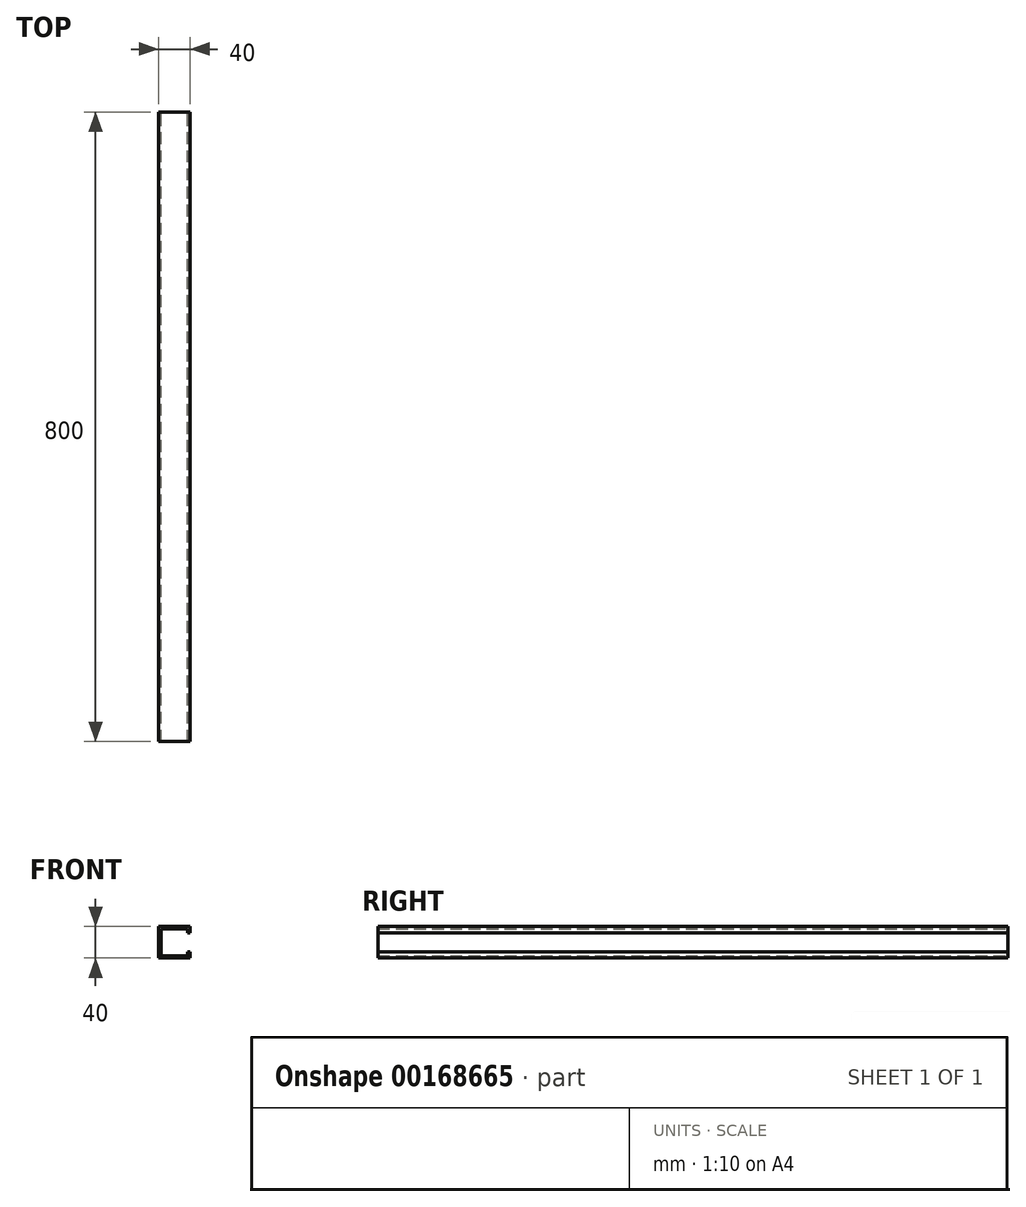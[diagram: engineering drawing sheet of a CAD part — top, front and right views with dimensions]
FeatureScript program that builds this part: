
annotation { "Feature Type Name" : "Feature", "Feature Type Description" : "" }
export const myFeature = defineFeature(function(context is Context, id is Id, definition is map)
    precondition{}
    {
        {
            var Q0;
            Q0=qCreatedBy(makeId("Front.planeOp"),FACE);
            var sketch = newSketch(context, id + "F0", { "sketchPlane" : qUnion([Q0])});
            skLineSegment(sketch, "E0.bottom", {"start": v(20, 20) * mm, "end": v(-20, 20) * mm});
            skLineSegment(sketch, "E0.top", {"start": v(20, -20) * mm, "end": v(-20, -20) * mm});
            skLineSegment(sketch, "E0.right", {"start": v(-20, 20) * mm, "end": v(-20, -20) * mm});
            skPoint(sketch, "E0.middle", {"position": v(0, 0) * mm});
            skLineSegment(sketch, "E1.0", {"start": v(17, -17) * mm, "end": v(-17, -17) * mm});
            skLineSegment(sketch, "E1.1", {"start": v(-17, 17) * mm, "end": v(-17, -17) * mm});
            skLineSegment(sketch, "E1.2", {"start": v(17, 17) * mm, "end": v(-17, 17) * mm});
            skLineSegment(sketch, "E2", {"start": v(17, 17) * mm, "end": v(17, 12) * mm});
            skLineSegment(sketch, "E3", {"start": v(17, 12) * mm, "end": v(20, 12) * mm});
            skLineSegment(sketch, "E4", {"start": v(20, -12) * mm, "end": v(17, -12) * mm});
            skLineSegment(sketch, "E5", {"start": v(17, -12) * mm, "end": v(17, -17) * mm});
            skLineSegment(sketch, "E6", {"start": v(20, 20) * mm, "end": v(20, 12) * mm});
            skLineSegment(sketch, "E7", {"start": v(20, -20) * mm, "end": v(20, -12) * mm});
            skSolve(sketch);
        }
        {
            var Q0;
            Q0=makeQuery(id+"F0.imprint","IMPRINT",FACE,{"disambiguationData":[TD([[makeQuery(id+"F0.imprint","IMPRINT",EDGE,{"derivedFrom":sQuery(id+"F0.wireOp",EDGE,"E0.bottom")}),1.0]])]});
            extrude(context, id + "F1", {"entities" : qUnion([Q0]), "depth" : 800 * mm});
        }
    });
